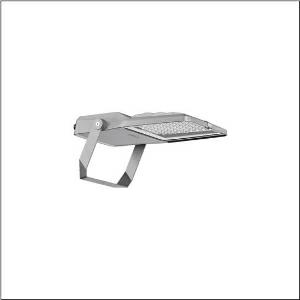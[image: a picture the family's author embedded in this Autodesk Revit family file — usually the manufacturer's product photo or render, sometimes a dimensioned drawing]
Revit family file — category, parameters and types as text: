
# Revit family: floodlight_fl_21_mini___pl33t_5xa7776c2f1a_ac63
name_source: partatom
category: Lighting Fixtures
units: mm (PartAtom-declared; Revit-internal decimal feet)

## family parameters
Cut with Voids When Loaded = No
Host = Face
Light Source = No
Part Type = Normal
Room Calculation Point = No
Round Connector Dimension = Use Diameter
Shared = No

## types (1)
- --- (1 x LED, 12050 lm, 89 W, 3000K)
    Apparent Load = 89 VA
    CIE Flux Codes = 26 75 99 100 100
    Color Rendering = 70
    Color Temperature = 3000K
    Default Elevation = 1800 mm
    Description = Floodlight FL 21 mini, floodlight, primary light control with lens, of PMMA, primary optical cover: protective disc, of toughened safety glass, transparent, light distribution: PL33T, light emission: direct distribution, installation type: surface-mounted, LED, High Power LED, rated luminous flux: 12.050lm, luminous efficacy: 135lm/W, light colour: 730, colour temperature: 3000K, control gear: Smart Interface (Zhaga), control: flexible luminous flux parameterisation, time-dependent luminous flux control, constant luminous flux control, overheat protection, pre-setting: logarithmic dimming characteristic, with terminal, 6-pole, mains connection: 220..240V, AC, 50/60Hz, start of lifetime: 89W, end of service life: 94W, reduction: 43W, luminaire housing, of diecast aluminium, powder-coated, SITECO metallic grey (DB 702S), corrosivity category C5 mid according to DIN EN ISO 12944, suitable for swimming pools, chlorine-resistant, sealing non-destructively replaceable, mounting bracket, of steel, galvanised, powder-coated, SITECO metallic grey (DB 702S), Smart Interface below and above, protection rating (complete): IP66, insulation class (complete): insulation class II (safety insulation), certification: CE, ENEC, VDE, protection symbol: D, impact resistance: IK08, permissible operating ambient temperature: -40..+40°C, permissible operating ambient temperature for outdoor applications: -40..+50°C, standard: DIN EN 12944, LABS conformity tested according to VDMA 24364:2018-05, packaging unit: 1 piece

Light Distribution: PL33T
    Height = 70 mm
    Lamp = 1 x LED
    Lamp Light Flux = 12050 lm
    Lamp Power = 89 W
    Lamp count = 1
    Length = 485 mm
    Luminous efficacy = 135 lm/W
    Manufacturer = Siteco
    ModVariant = No
    Model = 5XA7776C2F1A
    Number of Poles = 1
    OnlyDefault = Yes
    Power Factor = 1
    Product Name = Floodlight FL 21 mini | PL33T
    Product group = floodlight | pylon annexe
    ProductGroupID = 6201
    Protection Class = Protection class II
    Protection Degree = IP 66
    RLX_Detail_Level = 1
    RLX_Emergency_Light_Flux = 0 lm
    RLX_Emergency_Type = 0
    RLX_Emergency_Type_DB = No
    RlxData = <blob elided: 96105 chars, md5=ea43d82b>
    Socket = socket
    Standby Power = 0 W
    System Light Flux = 12050 lm
    System Power = 89 W
    Type Comments = factory setting: luminous flux: 100 % | dim-lin: 254 | 456 mA
    Type Image = l_1006845.jpg
    URL = http://relux.com
    VarID = @adj_147999
    Voltage = 0 V
    Weight = 0.00 kg
    Width = 337 mm

## geometry (parser evidence)
native form markers: Blend x4, Sweep x12
no freeform markers — native parametric forms only
